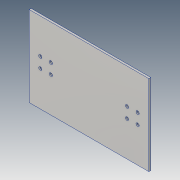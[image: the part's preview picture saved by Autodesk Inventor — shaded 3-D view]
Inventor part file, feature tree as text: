
AUTODESK INVENTOR PART (.ipt)
format: ipt  version: 2016 (Build 200138000, 138)  size: 108,032 bytes
history: native  units: in
note: dims shown in document units (in); Inventor stores cm internally (conversion verified against a paired STEP export)
features: extrude x1, hole x1, pattern_linear x1, plane x1, mirror x1, sketch x1
ambient origin geometry x8: Origin, YZ Plane, XZ Plane, XY Plane, X Axis, Y Axis, Z Axis, Center Point
bodies: Solid1 (feature_tree)
feature tree (6):
  extrude  "Extrusion1"  Depth=7.8346in
  hole  "Hole1"  [1 undecoded]
  pattern_linear  "Rectangular Pattern1"  Spacing1=1.0969in  [1 undecoded]
  plane  "Work Plane1"
  mirror  "Mirror1"
  sketch  "Sketch1"  dims[d0=11.6535in d1=7.8346in d2=0.7874in d4=1.0236in d5=0.7874in d7=1.0236in d10=1.0969in d12=0.1969in d13=0.0in d14=0.1969in d24=0.3937in d25=0.3937in d17=0.1772in d18=0.2362in d19=0.315in d20=0.0787in d21=90.0deg d22=0.315in d23=0.8108in d26=0.7874in d28=1.0236in d29=0.7874in d31=1.0236in]
note: 2 required parameter values undecoded (feature->parameter linkage not recoverable at this tier; creation-order binding heuristic only, values carry confidence <= 0.55)
